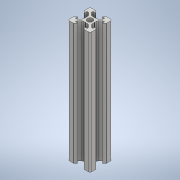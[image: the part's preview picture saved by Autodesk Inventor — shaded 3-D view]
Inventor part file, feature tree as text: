
AUTODESK INVENTOR PART (.ipt)
format: ipt  version: 2020 (Build 240168000, 168)  size: 273,920 bytes
history: native  units: mm
features: other x1, extrude x1, sketch x1
ambient origin geometry x8: Origin, YZ Plane, XZ Plane, XY Plane, X Axis, Y Axis, Z Axis, Center Point
bodies: Body1 (feature_tree)
feature tree (3):
  other  "Твердое тело1"
  extrude  "Выдавливание1"  Depth=0.25mm
  sketch  "Эскиз1"
